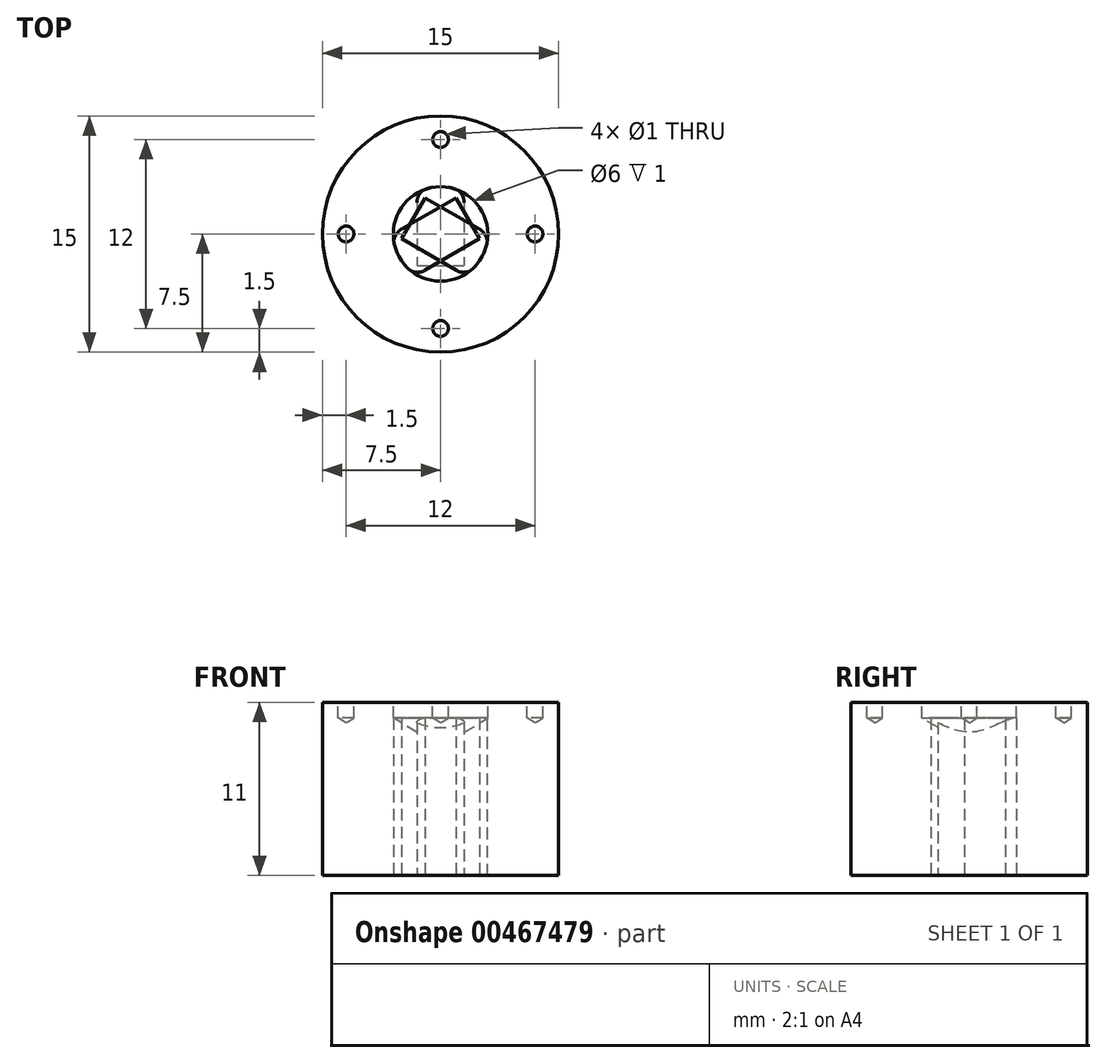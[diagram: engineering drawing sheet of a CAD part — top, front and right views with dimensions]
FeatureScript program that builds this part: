
annotation { "Feature Type Name" : "Feature", "Feature Type Description" : "" }
export const myFeature = defineFeature(function(context is Context, id is Id, definition is map)
    precondition{}
    {
        {
            var Q0;
            Q0=qCreatedBy(makeId("Top.planeOp"),FACE);
            var sketch = newSketch(context, id + "F0", { "sketchPlane" : qUnion([Q0])});
            skLineSegment(sketch, "E0.bottom", {"start": v(-1.5, 3) * mm, "end": v(1.5, 3) * mm});
            skLineSegment(sketch, "E0.top", {"start": v(-1.5, -2) * mm, "end": v(1.5, -2) * mm});
            skLineSegment(sketch, "E0.left", {"start": v(-1.5, 3) * mm, "end": v(-1.5, -2) * mm});
            skLineSegment(sketch, "E0.right", {"start": v(1.5, 3) * mm, "end": v(1.5, -2) * mm});
            skSolve(sketch);
        }
        {
            var Q0;
            Q0=makeQuery(id+"F0.imprint","IMPRINT",FACE,{"disambiguationData":[TD([[makeQuery(id+"F0.imprint","IMPRINT",EDGE,{"derivedFrom":sQuery(id+"F0.wireOp",EDGE,"E0.bottom")}),-1.0]])]});
            extrude(context, id + "F1", {"entities" : qUnion([Q0]), "depth" : 10 * mm});
        }
        {
            var Q0;
            Q0=makeQuery(id+"F1.opExtrude","SWEPT_EDGE",EDGE,{"disambiguationData":[OSD([sQuery(id+"F0.wireOp",EDGE,"E0.bottom"),sQuery(id+"F0.wireOp",EDGE,"E0.left")])]});
            var Q1;
            Q1=makeQuery(id+"F1.opExtrude","SWEPT_EDGE",EDGE,{"disambiguationData":[OSD([sQuery(id+"F0.wireOp",EDGE,"E0.bottom"),sQuery(id+"F0.wireOp",EDGE,"E0.right")])]});
            fillet(context, id + "F2", {"entities" : qUnion([Q0, Q1]), "radius" : 1 * mm, "tangentPropagation" : true, "allowEdgeOverflow" : false});
        }
        {
            var Q0;
            Q0=qCreatedBy(makeId("Right.planeOp"),FACE);
            var sketch = newSketch(context, id + "F3", { "sketchPlane" : qUnion([Q0])});
            skLineSegment(sketch, "E1", {"start": v(0, 12.33) * mm, "end": v(0, -2.39) * mm});
            skSolve(sketch);
        }
        {
            var Q0;
            Q0=makeQuery(id+"F1.opExtrude","SWEPT_BODY",BODY,{"disambiguationData":[OSD([sQuery(id+"F0.wireOp",EDGE,"E0.bottom"),sQuery(id+"F0.wireOp",EDGE,"E0.top"),sQuery(id+"F0.wireOp",EDGE,"E0.left"),sQuery(id+"F0.wireOp",EDGE,"E0.right")])]});
            var Q1;
            Q1=sQuery(id+"F3.wireOp",EDGE,"E1");
            circularPattern(context, id + "F4", {"entities" : qUnion([Q0]), "axis" : qUnion([Q1]), "angle" : 240 * degree, "instanceCount" : 3, "equalSpace" : true});
        }
        {
            var Q0;
            Q0=qCreatedBy(makeId("Top.planeOp"),FACE);
            var sketch = newSketch(context, id + "F5", { "sketchPlane" : qUnion([Q0])});
            skCircle(sketch, "E2", {"center": v(0, 0) * mm, "radius": 7.5 * mm});
            skSolve(sketch);
        }
        {
            var Q0;
            Q0 = qSketchRegion(id + "F5", true);
            extrude(context, id + "F6", {"entities" : qUnion([Q0]), "depth" : 11 * mm});
        }
        {
            var Q0;
            Q0=makeQuery(id+"F1.opExtrude","SWEPT_BODY",BODY,{"disambiguationData":[OSD([sQuery(id+"F0.wireOp",EDGE,"E0.bottom"),sQuery(id+"F0.wireOp",EDGE,"E0.top"),sQuery(id+"F0.wireOp",EDGE,"E0.left"),sQuery(id+"F0.wireOp",EDGE,"E0.right")])]});
            var Q1;
            Q1=makeQuery(id+"F6.opExtrude","SWEPT_BODY",BODY,{"disambiguationData":[OSD([sQuery(id+"F5.wireOp",EDGE,"E2")])]});
            booleanBodies(context, id + "F7", {"operationType" : BooleanOperationType.SUBTRACTION, "tools" : qUnion([Q0]), "targets" : qUnion([Q1])});
        }
        {
            var Q0;
            Q0=makeQuery(id+"F6.opExtrude","CAP_FACE",FACE,{"disambiguationData":[OSD([sQuery(id+"F5.wireOp",EDGE,"E2")])],"isStart":false});
            var sketch = newSketch(context, id + "F8", { "sketchPlane" : qUnion([Q0])});
            skPoint(sketch, "E3", {"position": v(0, 0) * mm});
            skPoint(sketch, "E4", {"position": v(-6, 0) * mm});
            skPoint(sketch, "E5", {"position": v(6, 0) * mm});
            skPoint(sketch, "E6", {"position": v(0, 6) * mm});
            skPoint(sketch, "E7", {"position": v(0, -6) * mm});
            skSolve(sketch);
        }
        {
            var Q0;
            Q0=sQuery(id+"F8.wireOp",VERTEX,"E4");
            var Q1;
            Q1=sQuery(id+"F8.wireOp",VERTEX,"E5");
            var Q2;
            Q2=sQuery(id+"F8.wireOp",VERTEX,"E6");
            var Q3;
            Q3=sQuery(id+"F8.wireOp",VERTEX,"E7");
            var Q4;
            Q4=makeQuery(id+"F6.opExtrude","SWEPT_BODY",BODY,{"disambiguationData":[OSD([sQuery(id+"F5.wireOp",EDGE,"E2")])]});
            hole(context, id + "F9", {"style" : HoleStyle.SIMPLE, "endStyle" : HoleEndStyle.BLIND, "holeDiameter" : 1 * mm, "holeDepth" : 1 * mm, "isTappedThrough" : true, "tappedDepth" : 12 * mm, "tapClearance" : 3, "locations" : qUnion([Q0, Q1, Q2, Q3]), "scope" : qUnion([Q4])});
        }
        {
            var Q0;
            Q0=sQuery(id+"F8.wireOp",VERTEX,"E3");
            var Q1;
            Q1=makeQuery(id+"F6.opExtrude","SWEPT_BODY",BODY,{"disambiguationData":[OSD([sQuery(id+"F5.wireOp",EDGE,"E2")])]});
            hole(context, id + "F10", {"style" : HoleStyle.SIMPLE, "endStyle" : HoleEndStyle.BLIND, "holeDiameter" : 6 * mm, "holeDepth" : 1 * mm, "isTappedThrough" : true, "tappedDepth" : 12 * mm, "tapClearance" : 3, "locations" : qUnion([Q0]), "scope" : qUnion([Q1])});
        }
    });
